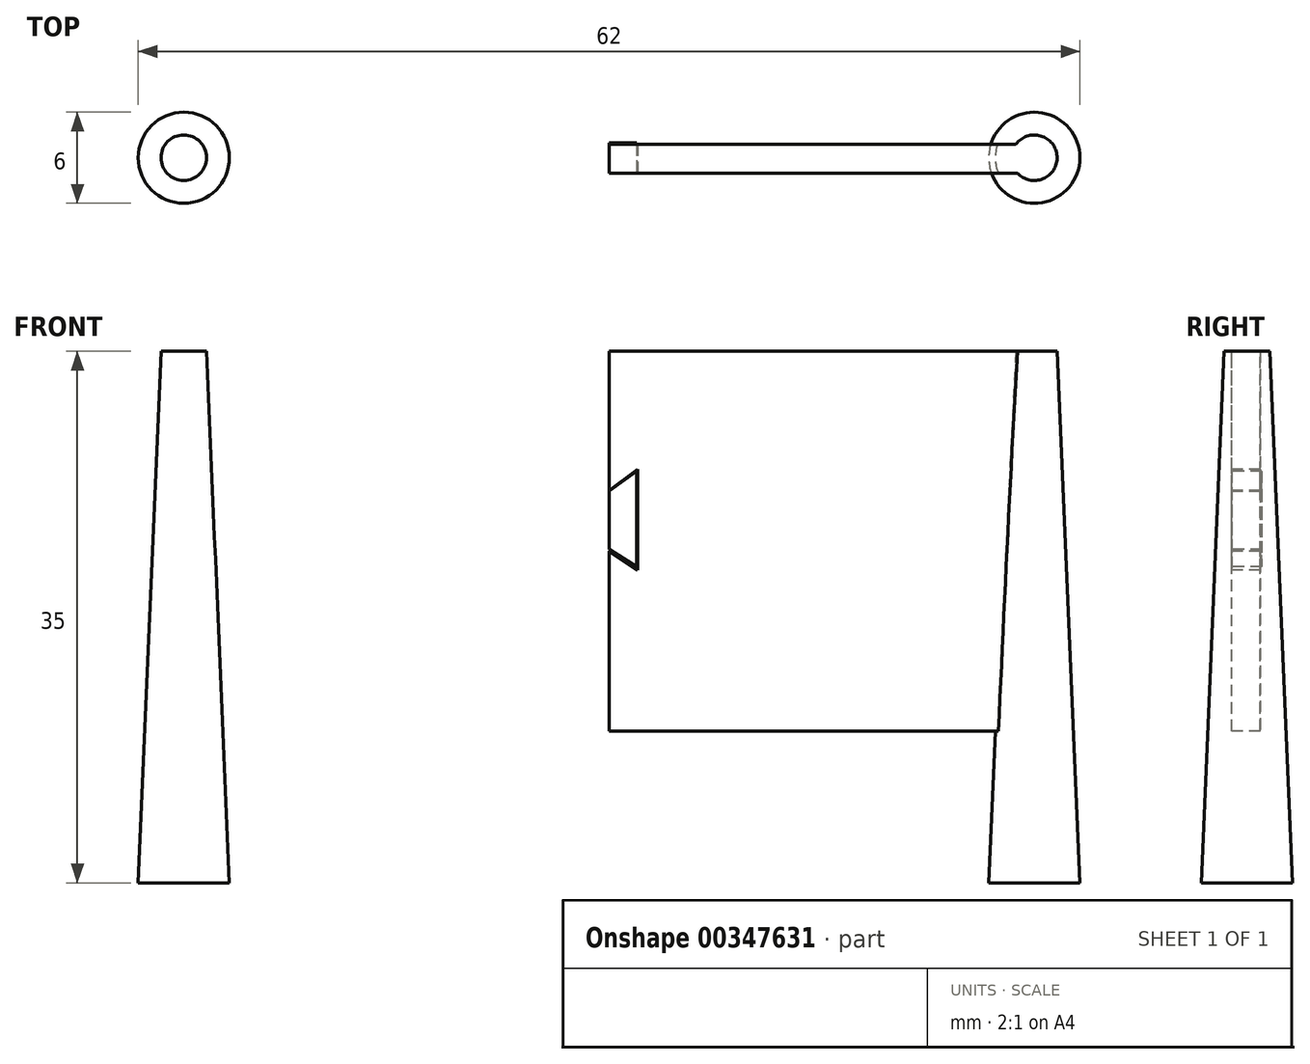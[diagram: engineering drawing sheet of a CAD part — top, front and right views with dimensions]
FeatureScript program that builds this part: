
annotation { "Feature Type Name" : "Feature", "Feature Type Description" : "" }
export const myFeature = defineFeature(function(context is Context, id is Id, definition is map)
    precondition{}
    {
        {
            var Q0;
            Q0=qCreatedBy(makeId("Top.planeOp"),FACE);
            var sketch = newSketch(context, id + "F0", { "sketchPlane" : qUnion([Q0])});
            skCircle(sketch, "E0", {"center": v(28, 0) * mm, "radius": 3 * mm});
            skCircle(sketch, "E1.MirrorC", {"center": v(-28, 0) * mm, "radius": 3 * mm});
            skSolve(sketch);
        }
        {
            var Q0;
            Q0=qCreatedBy(makeId("Top.planeOp"),FACE);
            cPlane(context, id + "F1", {"entities" : qUnion([Q0]), "cplaneType" : CPlaneType.OFFSET, "offset" : 35 * mm, "width" : 150 * mm, "height" : 150 * mm});
        }
        {
            var Q0;
            Q0=qCreatedBy(id+"F1.planeOp",FACE);
            var sketch = newSketch(context, id + "F2", { "sketchPlane" : qUnion([Q0])});
            skCircle(sketch, "E2", {"center": v(28, 0) * mm, "radius": 1.5 * mm});
            skCircle(sketch, "E3.MirrorC", {"center": v(-28, 0) * mm, "radius": 1.5 * mm});
            skSolve(sketch);
        }
        {
            var Q0;
            Q0=makeQuery(id+"F0.imprint","IMPRINT",FACE,{"disambiguationData":[TD([[makeQuery(id+"F0.imprint","IMPRINT",EDGE,{"derivedFrom":sQuery(id+"F0.wireOp",EDGE,"E0")}),1.0]])]});
            var Q1;
            Q1=makeQuery(id+"F2.imprint","IMPRINT",FACE,{"disambiguationData":[TD([[makeQuery(id+"F2.imprint","IMPRINT",EDGE,{"derivedFrom":sQuery(id+"F2.wireOp",EDGE,"E2")}),1.0]])]});
            loft(context, id + "F3", {"sheetProfilesArray" : [{ "sheetProfileEntities" : qUnion([Q0]) }, { "sheetProfileEntities" : qUnion([Q1]) }]});
        }
        {
            var Q0;
            Q0=qCreatedBy(id+"F1.planeOp",FACE);
            var sketch = newSketch(context, id + "F4", { "sketchPlane" : qUnion([Q0])});
            skLineSegment(sketch, "E4", {"start": v(27, 0.88) * mm, "end": v(0, 0.88) * mm});
            skLineSegment(sketch, "E5", {"start": v(0, 0.88) * mm, "end": v(0, -1.01) * mm});
            skLineSegment(sketch, "E6", {"start": v(0, -1.01) * mm, "end": v(27, -1.01) * mm});
            skLineSegment(sketch, "E7", {"start": v(27, 0.88) * mm, "end": v(27, -1.01) * mm});
            skLineSegment(sketch, "E8.MirrorCS", {"start": v(-27, 0.88) * mm, "end": v(0, 0.88) * mm});
            skLineSegment(sketch, "E9.MirrorCS", {"start": v(0, -1.01) * mm, "end": v(-27, -1.01) * mm});
            skLineSegment(sketch, "E10.MirrorCS", {"start": v(-27, 0.88) * mm, "end": v(-27, -1.01) * mm});
            skSolve(sketch);
        }
        {
            var Q0;
            Q0=makeQuery(id+"F4.imprint","IMPRINT",FACE,{"disambiguationData":[TD([[makeQuery(id+"F4.imprint","IMPRINT",EDGE,{"derivedFrom":sQuery(id+"F4.wireOp",EDGE,"E4")}),1.0]])]});
            extrude(context, id + "F5", {"entities" : qUnion([Q0]), "operationType" : NewBodyOperationType.ADD, "oppositeDirection" : true, "depth" : 25 * mm});
        }
        {
            var Q0;
            Q0=qCreatedBy(makeId("Top.planeOp"),FACE);
            var sketch = newSketch(context, id + "F6", { "sketchPlane" : qUnion([Q0])});
            skCircle(sketch, "E11", {"center": v(-28, 0) * mm, "radius": 3 * mm});
            skSolve(sketch);
        }
        {
            var Q0;
            Q0=qCreatedBy(id+"F1.planeOp",FACE);
            var sketch = newSketch(context, id + "F7", { "sketchPlane" : qUnion([Q0])});
            skCircle(sketch, "E12", {"center": v(-28, 0) * mm, "radius": 1.5 * mm});
            skSolve(sketch);
        }
        {
            var Q0;
            Q0=makeQuery(id+"F7.imprint","IMPRINT",FACE,{"disambiguationData":[TD([[makeQuery(id+"F7.imprint","IMPRINT",EDGE,{"derivedFrom":sQuery(id+"F7.wireOp",EDGE,"E12")}),1.0]])]});
            var Q1;
            Q1=makeQuery(id+"F6.imprint","IMPRINT",FACE,{"disambiguationData":[TD([[makeQuery(id+"F6.imprint","IMPRINT",EDGE,{"derivedFrom":sQuery(id+"F6.wireOp",EDGE,"E11")}),1.0]])]});
            loft(context, id + "F8", {"sheetProfilesArray" : [{ "sheetProfileEntities" : qUnion([Q0]) }, { "sheetProfileEntities" : qUnion([Q1]) }]});
        }
        {
            var Q0;
            Q0=qCreatedBy(id+"F1.planeOp",FACE);
            var sketch = newSketch(context, id + "F9", { "sketchPlane" : qUnion([Q0])});
            skLineSegment(sketch, "E13", {"start": v(0, 0.87) * mm, "end": v(-27.4, 0.87) * mm});
            skLineSegment(sketch, "E14", {"start": v(-27.4, 0.87) * mm, "end": v(-27.4, -1.02) * mm});
            skLineSegment(sketch, "E15", {"start": v(-27.4, -1.02) * mm, "end": v(0, -1.02) * mm});
            skSolve(sketch);
        }
        {
            var Q0;
            Q0=qCreatedBy(id+"F1.planeOp",FACE);
            var sketch = newSketch(context, id + "F10", { "sketchPlane" : qUnion([Q0])});
            skLineSegment(sketch, "E16", {"start": v(0, -1.02) * mm, "end": v(0, 0.87) * mm});
            skSolve(sketch);
        }
        {
            var Q0;
            Q0=sQuery(id+"F10.wireOp",EDGE,"E16");
            var Q1;
            Q1=sQuery(id+"F9.wireOp",EDGE,"E13");
            var Q2;
            Q2=sQuery(id+"F9.wireOp",EDGE,"E14");
            var Q3;
            Q3=sQuery(id+"F9.wireOp",EDGE,"E15");
            extrude(context, id + "F11", {"bodyType" : ToolBodyType.SURFACE, "surfaceEntities" : qUnion([Q0, Q1, Q2, Q3]), "oppositeDirection" : true, "depth" : 25 * mm});
        }
        {
            var Q0;
            Q0=makeQuery(id+"F5.opExtrude","SWEPT_FACE",FACE,{"disambiguationData":[OSD([sQuery(id+"F4.wireOp",EDGE,"E6")])]});
            var sketch = newSketch(context, id + "F12", { "sketchPlane" : qUnion([Q0])});
            skLineSegment(sketch, "E17", {"start": v(0, 25.85) * mm, "end": v(1.87, 27.22) * mm});
            skLineSegment(sketch, "E18", {"start": v(1.87, 27.22) * mm, "end": v(1.87, 20.59) * mm});
            skLineSegment(sketch, "E19", {"start": v(1.87, 20.59) * mm, "end": v(0, 21.84) * mm});
            skLineSegment(sketch, "E20", {"start": v(0, 25.85) * mm, "end": v(0, 21.84) * mm});
            skSolve(sketch);
        }
        {
            var Q0;
            Q0=makeQuery(id+"F12.imprint","IMPRINT",FACE,{"disambiguationData":[TD([[makeQuery(id+"F12.imprint","IMPRINT",EDGE,{"derivedFrom":sQuery(id+"F12.wireOp",EDGE,"E17")}),-1.0]])]});
            extrude(context, id + "F13", {"entities" : qUnion([Q0]), "operationType" : NewBodyOperationType.REMOVE, "oppositeDirection" : true, "depth" : 25 * mm});
        }
        {
            var Q0;
            Q0=makeQuery(id+"F11.opExtrude","SWEPT_FACE",FACE,{"disambiguationData":[OSD([sQuery(id+"F9.wireOp",EDGE,"E15")])]});
            var sketch = newSketch(context, id + "F14", { "sketchPlane" : qUnion([Q0])});
            skLineSegment(sketch, "E21", {"start": v(0, 25.8) * mm, "end": v(-1.83, 27.1) * mm});
            skLineSegment(sketch, "E22", {"start": v(-1.83, 27.1) * mm, "end": v(-1.83, 20.83) * mm});
            skLineSegment(sketch, "E23", {"start": v(-1.83, 20.83) * mm, "end": v(0, 21.96) * mm});
            skLineSegment(sketch, "E24", {"start": v(0, 21.96) * mm, "end": v(0, 25.8) * mm});
            skSolve(sketch);
        }
        {
            var Q0;
            Q0=makeQuery(id+"F14.imprint","IMPRINT",FACE,{"disambiguationData":[TD([[makeQuery(id+"F14.imprint","IMPRINT",EDGE,{"derivedFrom":sQuery(id+"F14.wireOp",EDGE,"E21")}),1.0]])]});
            extrude(context, id + "F15", {"entities" : qUnion([Q0]), "depth" : 2 * mm});
        }
    });
